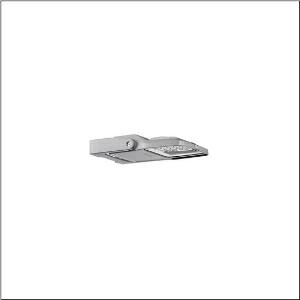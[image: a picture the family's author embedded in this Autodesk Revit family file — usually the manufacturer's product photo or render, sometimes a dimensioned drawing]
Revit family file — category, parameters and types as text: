
# Revit family: floodlight_fl_21_iq_micro___pl43_5xa7762a2a2a_df73
name_source: partatom
category: Lighting Fixtures
units: mm (PartAtom-declared; Revit-internal decimal feet)

## family parameters
Cut with Voids When Loaded = No
Host = Face
Light Source = No
Part Type = Normal
Room Calculation Point = No
Round Connector Dimension = Use Diameter
Shared = No

## types (1)
- --- (1 x LED, 3040 lm, 23.1 W, 3000K)
    Apparent Load = 23 VA
    CIE Flux Codes = 29 80 99 100 100
    Color Rendering = 70
    Color Temperature = 3000K
    Default Elevation = 1800 mm
    Description = Floodlight FL 21 iQ micro, floodlight, primary light control with lens, of PMMA, primary optical cover: protective disc, of toughened safety glass, transparent, light distribution: PL43, light emission: direct distribution, installation type: surface-mounted, lamps: LED, High Power LED, rated values: 3.040lm | 23,1W | 131,6lm/W (begin service life); end service life: 3.040lm | 23,8W; at 50% lumin. flux: 1.520lm | 11W | 138,2lm/W, colour temperature: 3000K, colour rendering: CRI > 70, light colour: 730, light setting 1 begin service life: 100% | 3.040lm | 23,1W | 131,6lm/W | 3.000K, light setting 1 end service life: 23,8W, further light settings possible, control: Auto-Match, Temp-Guard, Night-Set, Smart-Wire, Desk-Remote (wireless, voltage-free reading and setting of iQ features in the workshop via application-optimized NFC function/RFID function), optimised constant luminous flux control (CLO 2.0), Street-Remote, pre-setting: linear dimming characteristic, with terminal, 6-pole, mains connection: 220..240V, AC, 50/60Hz, luminaire housing, of diecast aluminium, powder-coated, SITECO metallic grey (DB 702S), corrosivity category C5 mid according to DIN EN ISO 12944suitable for swimming poolschlorine-resistant, sealing non-destructively replaceable, design bracket, of diecast aluminium, powder-coated, SITECO metallic grey (DB 702S), protection rating (complete): IP66, insulation class (complete): insulation class II (safety insulation), certification: CE, ENEC, VDE, protection symbol: D, impact resistance: IK07, permissible operating ambient temperature: -40..+40°C, permissible operating ambient temperature for outdoor applications: -40..+50°C, standard: DIN EN 12944, LABS conformity tested according to VDMA 24364:2018-05, packaging unit: 1 piece

Light Distribution: PL43
    Height = 65 mm
    Lamp = 1 x LED
    Lamp Light Flux = 3040 lm
    Lamp Power = 23.1 W
    Lamp count = 1
    Length = 312 mm
    Luminous efficacy = 132 lm/W
    Manufacturer = Siteco
    ModVariant = No
    Model = 5XA7762A2A2A
    Mounting Place = Wall
    Mounting Type = Surface mounted
    Number of Poles = 1
    OnlyDefault = Yes
    Power Factor = 1
    Product Name = Floodlight FL 21 iQ micro | PL43
    Product group = floodlight | wall mounted
    ProductGroupID = 2002
    Protection Class = Protection class II
    Protection Degree = IP 66
    RLX_Detail_Level = 1
    RLX_Emergency_Light_Flux = 0 lm
    RLX_Emergency_Type = 0
    RLX_Emergency_Type_DB = No
    RlxData = <blob elided: 97545 chars, md5=35c731c4>
    Socket = socket
    Standby Power = 0 W
    System Light Flux = 3040 lm
    System Power = 23 W
    Type Comments = factory setting: luminous flux: 100 % | dim-lin: 254 | 455 mA
    Type Image = l_1006878.jpg
    URL = http://relux.com
    VarID = @adj_177653
    Voltage = 0 V
    Weight = 0.00 kg
    Width = 230 mm

## geometry (parser evidence)
native form markers: Blend x4, Sweep x11
no freeform markers — native parametric forms only
